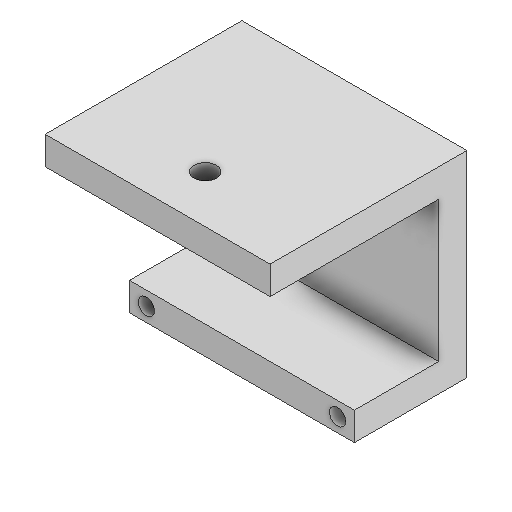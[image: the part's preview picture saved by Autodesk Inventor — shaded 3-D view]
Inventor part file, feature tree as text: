
AUTODESK INVENTOR PART (.ipt)
format: ipt  version: 2025.1 (Build 291241000, 241)  size: 133,120 bytes
history: native  units: mm
features: sketch x6, extrude x4, hole x2, other x1
ambient origin geometry x8: Origin, YZ Plane, XZ Plane, XY Plane, X Axis, Y Axis, Z Axis, Center Point
bodies: Body1 (feature_tree)
feature tree (13):
  other  "Bryła1"
  extrude  "Wyciągnięcie proste1"  Depth=40.0mm
  extrude  "Wyciągnięcie proste2"  Depth=30.0mm
  extrude  "Wyciągnięcie proste3"  Depth=5.0mm TaperAngle=0.0deg
  hole  "Otwór1"  [1 undecoded]
  extrude  "Wyciągnięcie proste4"  Depth=30.0mm TaperAngle=0.0deg
  hole  "Otwór2"  [1 undecoded]
  sketch  "Szkic1"
  sketch  "Szkic2"
  sketch  "Szkic5"
  sketch  "Szkic6"
  sketch  "Szkic7"
  sketch  "Szkic8"
note: 2 required parameter values undecoded (feature->parameter linkage not recoverable at this tier; creation-order binding heuristic only, values carry confidence <= 0.55)
